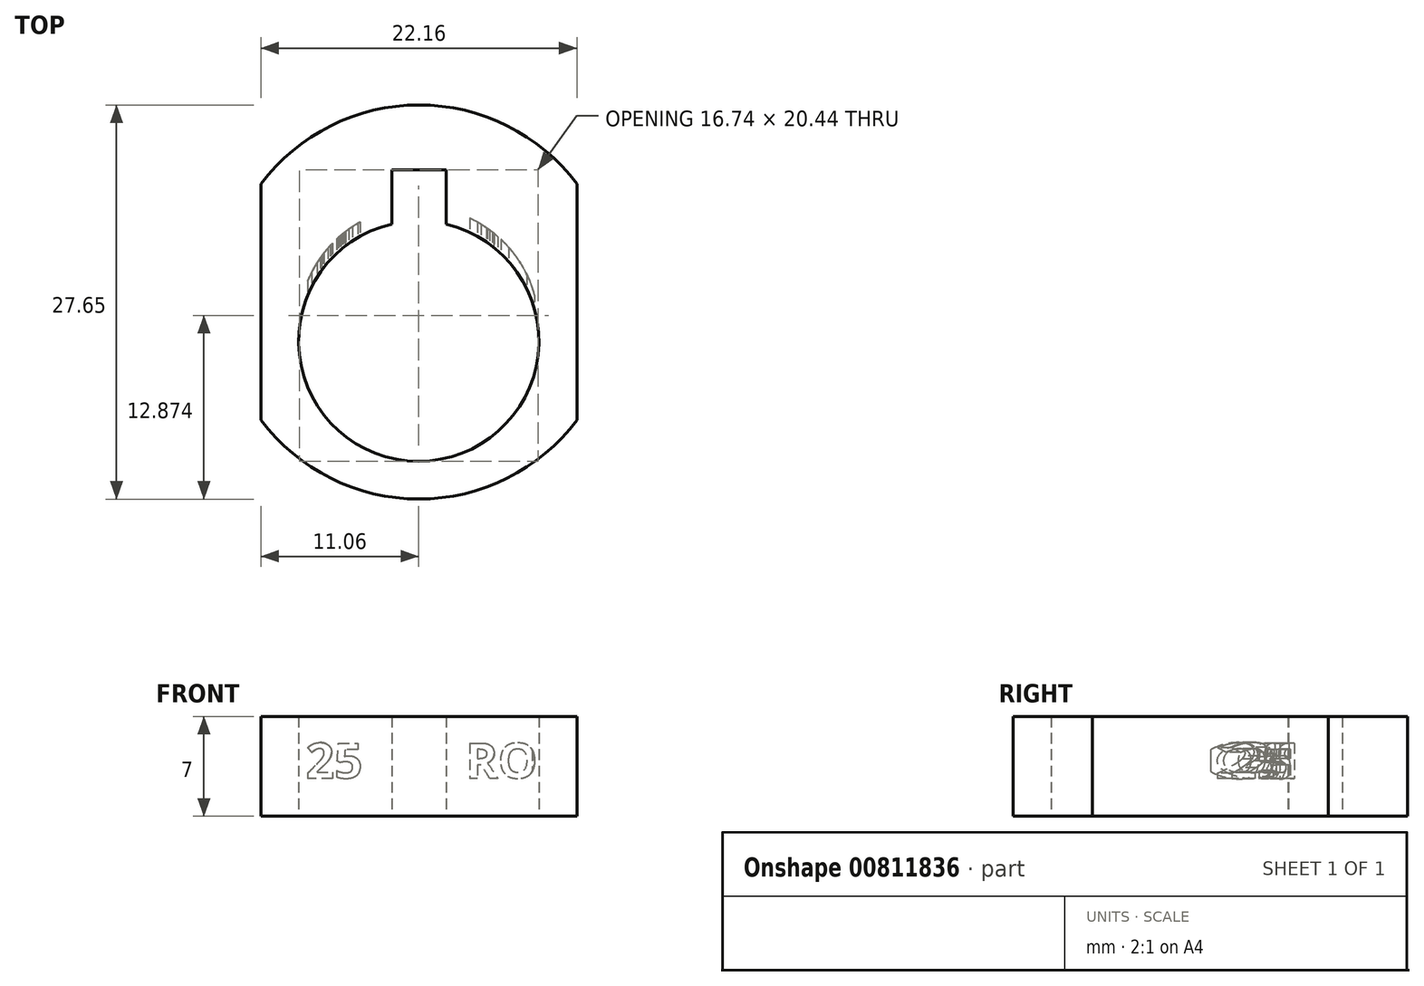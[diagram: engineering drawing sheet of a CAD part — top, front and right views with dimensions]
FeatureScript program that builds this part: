
annotation { "Feature Type Name" : "Feature", "Feature Type Description" : "" }
export const myFeature = defineFeature(function(context is Context, id is Id, definition is map)
    precondition{}
    {
        {
            var Q0;
            Q0=qCreatedBy(makeId("Top.planeOp"),FACE);
            var sketch = newSketch(context, id + "F0", { "sketchPlane" : qUnion([Q0])});
            skCircle(sketch, "E0", {"center": v(0, -2.75) * mm, "radius": 8.43 * mm});
            skSolve(sketch);
        }
        {
            var Q0;
            Q0=qCreatedBy(makeId("Top.planeOp"),FACE);
            var sketch = newSketch(context, id + "F1", { "sketchPlane" : qUnion([Q0])});
            skArc(sketch, "E1", {"start": v(-11.07, -8.27) * mm, "mid": v(0, -13.82) * mm, "end": v(11.08, -8.27) * mm});
            skLineSegment(sketch, "E2.right", {"start": v(-11.07, 8.27) * mm, "end": v(-11.07, -8.27) * mm});
            skLineSegment(sketch, "E3.right", {"start": v(11.07, 8.27) * mm, "end": v(11.08, -8.27) * mm});
            skArc(sketch, "E4.trimOffspring", {"start": v(11.07, 8.27) * mm, "mid": v(0, 13.83) * mm, "end": v(-11.08, 8.27) * mm});
            skArc(sketch, "E5", {"start": v(-1.9, 5.46) * mm, "mid": v(-0.04, -11.17) * mm, "end": v(1.9, 5.45) * mm});
            skLineSegment(sketch, "E6.top", {"start": v(1.9, 9.26) * mm, "end": v(-1.9, 9.26) * mm});
            skLineSegment(sketch, "E6.right", {"start": v(-1.9, 5.46) * mm, "end": v(-1.9, 9.26) * mm});
            skLineSegment(sketch, "E7", {"start": v(1.9, 9.26) * mm, "end": v(1.9, 5.45) * mm});
            skSolve(sketch);
        }
        {
            var Q0;
            Q0=makeQuery(id+"F1.imprint","IMPRINT",FACE,{"disambiguationData":[TD([[makeQuery(id+"F1.imprint","IMPRINT",EDGE,{"derivedFrom":sQuery(id+"F1.wireOp",EDGE,"E1")}),1.0]])]});
            extrude(context, id + "F2", {"entities" : qUnion([Q0]), "depth" : 7 * mm, "offsetDistance" : 25 * mm});
        }
        {
            var Q0;
            Q0=qCreatedBy(makeId("Front.planeOp"),FACE);
            var sketch = newSketch(context, id + "F3", { "sketchPlane" : qUnion([Q0])});
            skText(sketch, "E8", { "text": "25        RO", "fontName": "OpenSans-Bold.ttf"});
            const initialGuessF3  = {"E8": [-0.00793, 0.00266, 1, 0, 0.0025]};
            skSetInitialGuess(sketch, initialGuessF3);
            skSolve(sketch);
        }
        {
            var Q0;
            Q0 = qSketchRegion(id + "F3", true);
            var Q1;
            Q1=makeQuery(id+"F2.opExtrude","SWEPT_BODY",BODY,{"disambiguationData":[OSD([sQuery(id+"F1.wireOp",EDGE,"E1"),sQuery(id+"F1.wireOp",EDGE,"E2.right"),sQuery(id+"F1.wireOp",EDGE,"E3.right"),sQuery(id+"F1.wireOp",EDGE,"E4.trimOffspring"),sQuery(id+"F1.wireOp",EDGE,"E5"),sQuery(id+"F1.wireOp",EDGE,"E6.top"),sQuery(id+"F1.wireOp",EDGE,"E6.right"),sQuery(id+"F1.wireOp",EDGE,"E7")])]});
            extrude(context, id + "F4", {"entities" : qUnion([Q0]), "operationType" : NewBodyOperationType.REMOVE, "endBound" : BoundingType.UP_TO_BODY, "oppositeDirection" : true, "depth" : 15.6 * mm, "endBoundEntityBody" : qUnion([Q1]), "hasOffset" : true, "offsetDistance" : -1 * mm});
        }
    });
